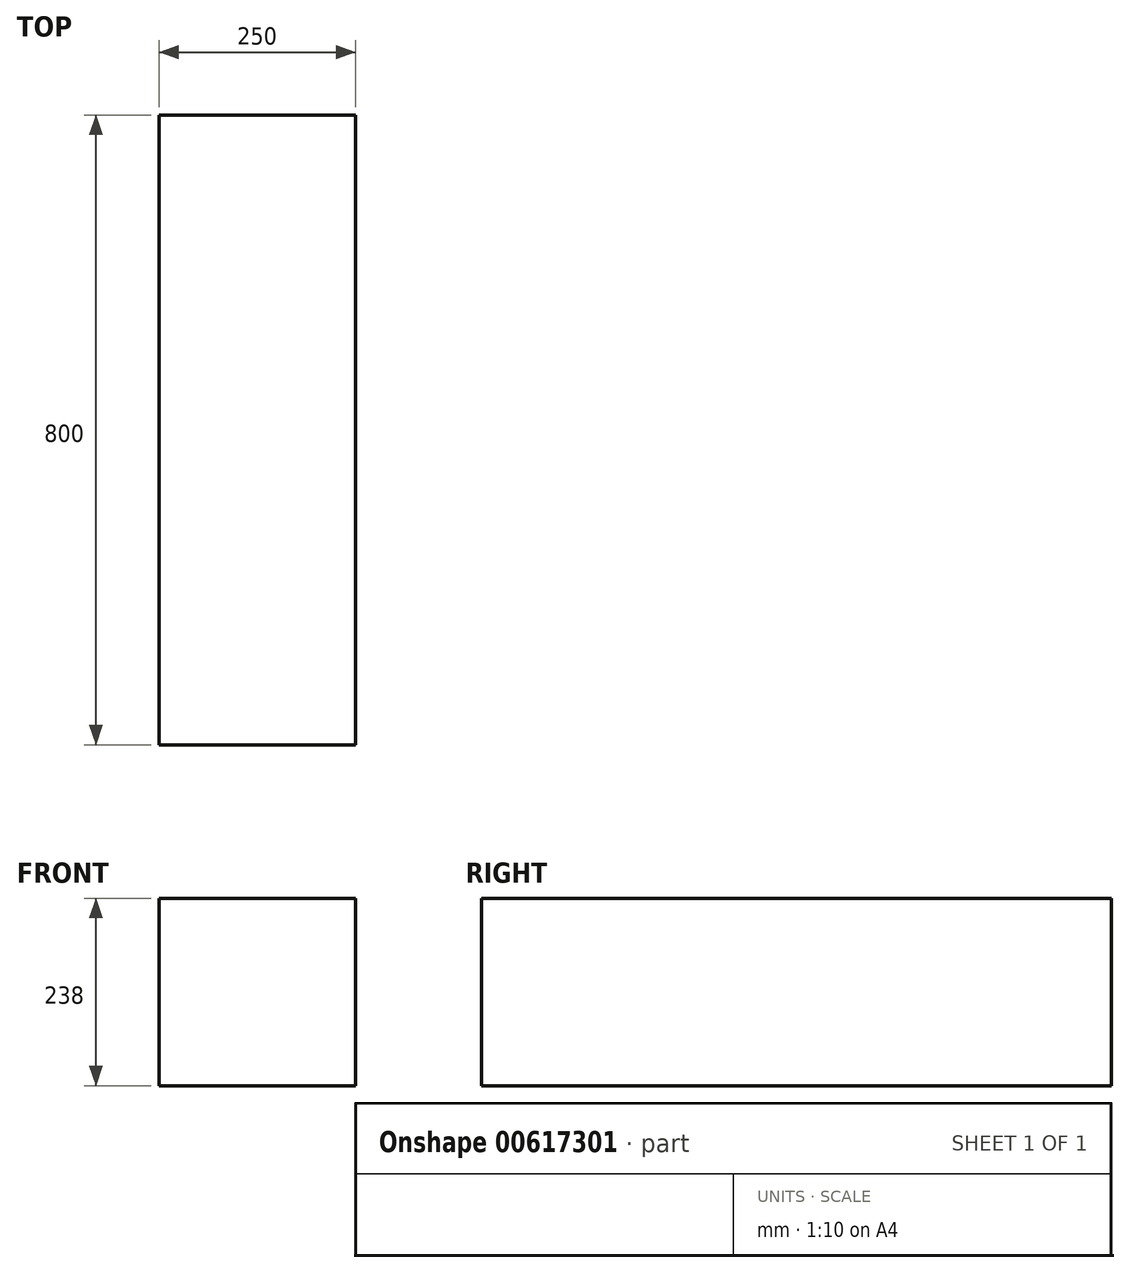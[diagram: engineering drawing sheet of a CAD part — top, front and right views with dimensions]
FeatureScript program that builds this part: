
annotation { "Feature Type Name" : "Feature", "Feature Type Description" : "" }
export const myFeature = defineFeature(function(context is Context, id is Id, definition is map)
    precondition{}
    {
        {
            var Q0;
            Q0=qCreatedBy(makeId("Top.planeOp"),FACE);
            var sketch = newSketch(context, id + "F0", { "sketchPlane" : qUnion([Q0])});
            skLineSegment(sketch, "E0.bottom", {"start": v(-6.76, 769.45) * mm, "end": v(243.24, 769.45) * mm});
            skLineSegment(sketch, "E0.top", {"start": v(-6.76, -30.55) * mm, "end": v(243.24, -30.55) * mm});
            skLineSegment(sketch, "E0.left", {"start": v(-6.76, 769.45) * mm, "end": v(-6.76, -30.55) * mm});
            skLineSegment(sketch, "E0.right", {"start": v(243.24, 769.45) * mm, "end": v(243.24, -30.55) * mm});
            skSolve(sketch);
        }
        {
            var Q0;
            Q0 = qSketchRegion(id + "F0", true);
            extrude(context, id + "F1", {"entities" : qUnion([Q0]), "depth" : 238 * mm, "offsetDistance" : 25 * mm});
        }
    });
